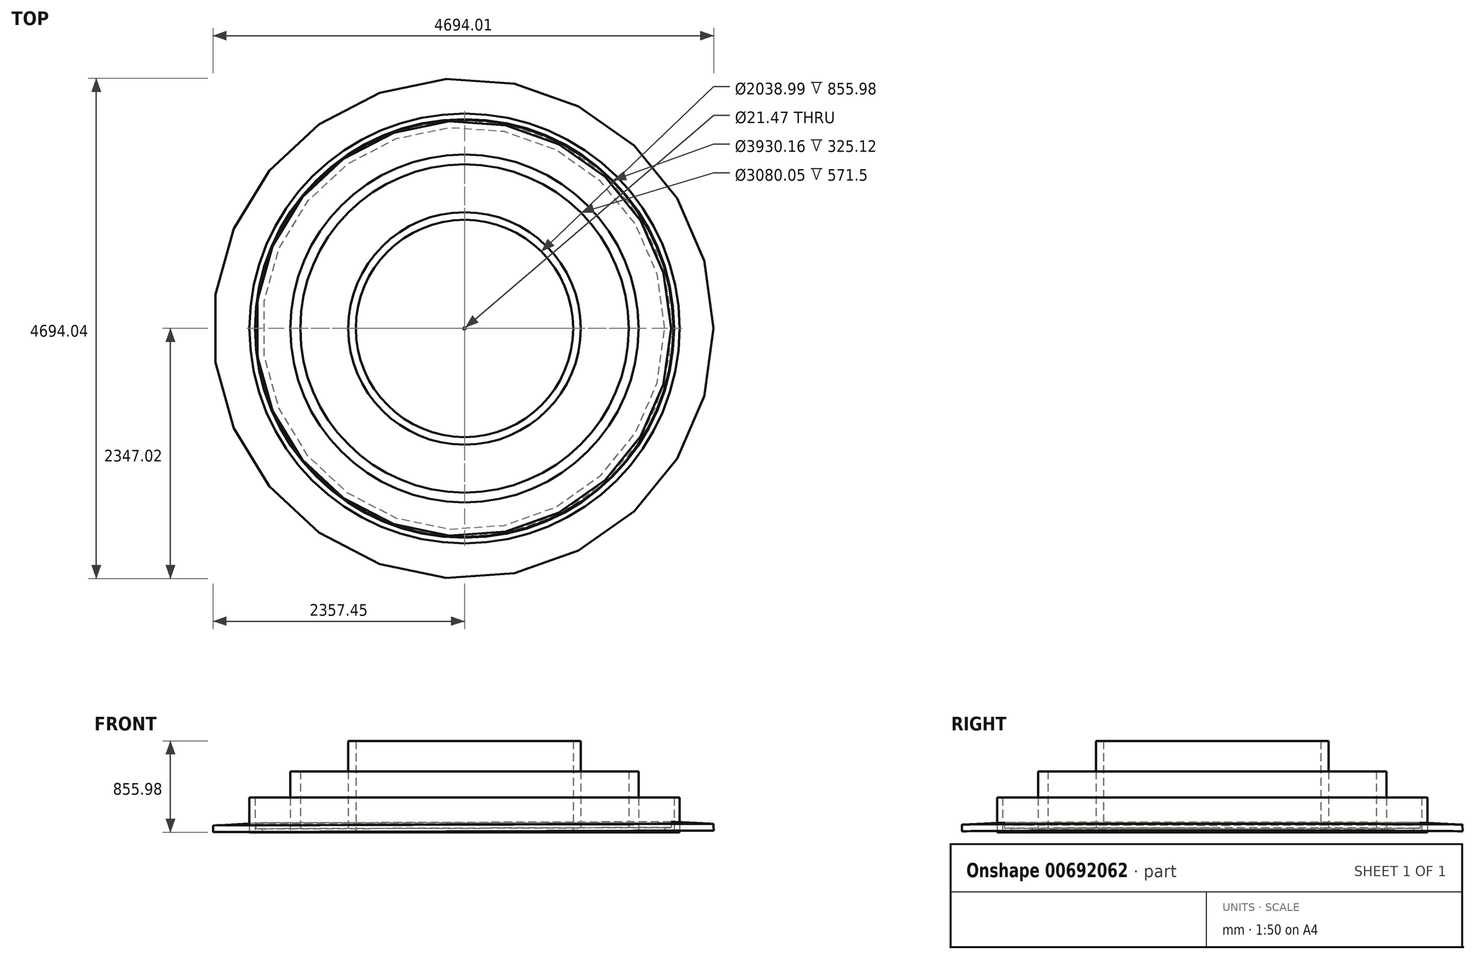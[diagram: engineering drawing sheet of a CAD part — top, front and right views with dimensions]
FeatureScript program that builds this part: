
annotation { "Feature Type Name" : "Feature", "Feature Type Description" : "" }
export const myFeature = defineFeature(function(context is Context, id is Id, definition is map)
    precondition{}
    {
        {
            var Q0;
            Q0=qCreatedBy(makeId("Front.planeOp"),FACE);
            var sketch = newSketch(context, id + "F0", { "sketchPlane" : qUnion([Q0])});
            skLineSegment(sketch, "E0", {"start": v(-346.13, 0.8) * mm, "end": v(-346.13, 28.74) * mm});
            skLineSegment(sketch, "E1", {"start": v(-346.13, 0.8) * mm, "end": v(1541.09, 0.8) * mm});
            skLineSegment(sketch, "E2", {"start": v(1541.09, 68.5) * mm, "end": v(1541.09, 103.08) * mm});
            skLineSegment(sketch, "E3", {"start": v(1541.09, 103.08) * mm, "end": v(1541.26, 50.06) * mm});
            skLineSegment(sketch, "E4", {"start": v(-346.13, 0.8) * mm, "end": v(-805.62, 0.8) * mm});
            skLineSegment(sketch, "E5", {"start": v(-805.62, 63.79) * mm, "end": v(-805.62, 0.8) * mm});
            skLineSegment(sketch, "E6", {"start": v(-805.62, 63.79) * mm, "end": v(-407.1, 85.65) * mm});
            skLineSegment(sketch, "E7", {"start": v(-407.1, 31.46) * mm, "end": v(-346.13, 28.74) * mm});
            skLineSegment(sketch, "E8", {"start": v(-407.1, 85.65) * mm, "end": v(-407.1, 31.46) * mm});
            skLineSegment(sketch, "E9", {"start": v(-407.1, 85.65) * mm, "end": v(1541.09, 85.65) * mm});
            skLineSegment(sketch, "E10", {"start": v(1541.09, 85.65) * mm, "end": v(1541.13, 88.58) * mm});
            skLineSegment(sketch, "E11", {"start": v(1541.13, 88.58) * mm, "end": v(-406.93, 88.58) * mm});
            skLineSegment(sketch, "E12", {"start": v(-407.1, 85.65) * mm, "end": v(-406.93, 88.58) * mm});
            skSolve(sketch);
        }
        {
            var Q0;
            Q0=makeQuery(id+"F0.imprint","IMPRINT",FACE,{"disambiguationData":[TD([[makeQuery(id+"F0.imprint","IMPRINT",EDGE,{"derivedFrom":sQuery(id+"F0.wireOp",EDGE,"E0")}),1.0]])]});
            var Q1;
            Q1=sQuery(id+"F0.wireOp",EDGE,"E3");
            revolve(context, id + "F1", {"entities" : qUnion([Q0]), "axis" : qUnion([Q1]), "revolveType" : RevolveType.FULL});
        }
        {
            var Q0;
            Q0=qCreatedBy(makeId("Top.planeOp"),FACE);
            var sketch = newSketch(context, id + "F2", { "sketchPlane" : qUnion([Q0])});
            skCircle(sketch, "E13", {"center": v(1551.83, 0) * mm, "radius": 2016.87 * mm});
            skCircle(sketch, "E14", {"center": v(1551.83, 0) * mm, "radius": 1965.08 * mm});
            skCircle(sketch, "E15", {"center": v(1551.83, 0) * mm, "radius": 1632.91 * mm});
            skCircle(sketch, "E16", {"center": v(1551.83, 0) * mm, "radius": 1540.03 * mm});
            skCircle(sketch, "E17", {"center": v(1551.83, 0) * mm, "radius": 1090.6 * mm});
            skCircle(sketch, "E18", {"center": v(1551.83, 0) * mm, "radius": 1019.5 * mm});
            skSolve(sketch);
        }
        {
            var Q0;
            Q0=makeQuery(id+"F2.imprint","IMPRINT",FACE,{"disambiguationData":[TD([[makeQuery(id+"F2.imprint","IMPRINT",EDGE,{"derivedFrom":sQuery(id+"F2.wireOp",EDGE,"E13")}),1.0]])]});
            extrude(context, id + "F3", {"entities" : qUnion([Q0]), "depth" : 325.12 * mm, "offsetDistance" : 25.4 * mm});
        }
        {
            var Q0;
            Q0=makeQuery(id+"F2.imprint","IMPRINT",FACE,{"disambiguationData":[TD([[makeQuery(id+"F2.imprint","IMPRINT",EDGE,{"derivedFrom":sQuery(id+"F2.wireOp",EDGE,"E15")}),1.0]])]});
            extrude(context, id + "F4", {"entities" : qUnion([Q0]), "depth" : 571.5 * mm, "offsetDistance" : 25.4 * mm});
        }
        {
            var Q0;
            Q0=makeQuery(id+"F2.imprint","IMPRINT",FACE,{"disambiguationData":[TD([[makeQuery(id+"F2.imprint","IMPRINT",EDGE,{"derivedFrom":sQuery(id+"F2.wireOp",EDGE,"E17")}),1.0]])]});
            extrude(context, id + "F5", {"entities" : qUnion([Q0]), "depth" : 855.98 * mm, "offsetDistance" : 25.4 * mm});
        }
        {
            var Q0;
            {var subQ0=sQuery(id+"F0.wireOp",EDGE,"E9");Q0=makeQuery(id+"F0.imprint","IMPRINT",FACE,{"disambiguationData":[TD([[makeQuery(id+"F0.imprint","IMPRINT",EDGE,{"derivedFrom":subQ0}),1.0]])]});}
            var Q1;
            Q1=makeQuery(id+"F5.opExtrude","SWEPT_FACE",FACE,{"disambiguationData":[OSD([sQuery(id+"F2.wireOp",EDGE,"E18")])]});
            revolve(context, id + "F6", {"surfaceOperationType" : NewSurfaceOperationType.NEW, "entities" : qUnion([Q0]), "axis" : qUnion([Q1]), "revolveType" : RevolveType.FULL});
        }
    });
